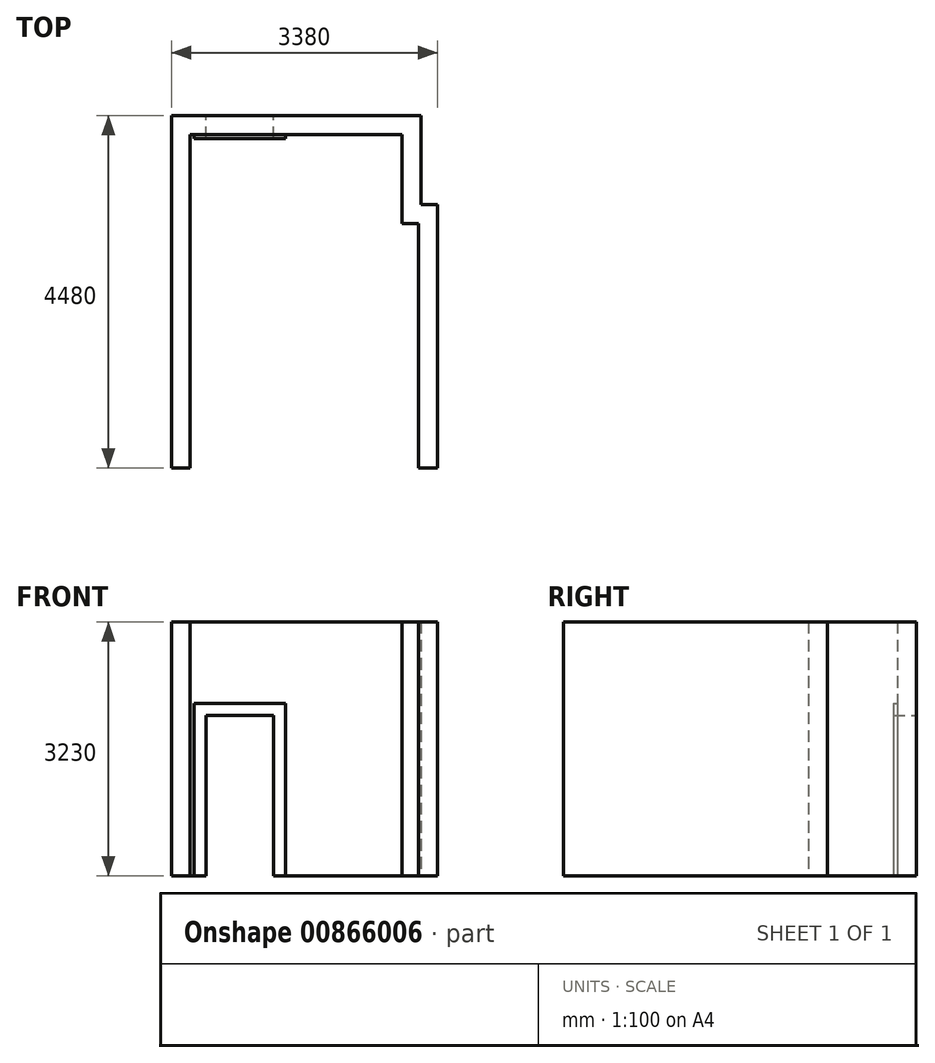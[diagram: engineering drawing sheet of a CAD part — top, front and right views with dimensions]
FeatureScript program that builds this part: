
annotation { "Feature Type Name" : "Feature", "Feature Type Description" : "" }
export const myFeature = defineFeature(function(context is Context, id is Id, definition is map)
    precondition{}
    {
        {
            var Q0;
            Q0=qCreatedBy(makeId("Top.planeOp"),FACE);
            var sketch = newSketch(context, id + "F0", { "sketchPlane" : qUnion([Q0])});
            skLineSegment(sketch, "E0.bottom", {"start": v(-3140, 4240) * mm, "end": v(-450, 4240) * mm});
            skLineSegment(sketch, "E0.top", {"start": v(-3140, 240) * mm, "end": v(-240, 240) * mm, "construction": true});
            skLineSegment(sketch, "E0.left", {"start": v(-3140, 4240) * mm, "end": v(-3140, 240) * mm});
            skLineSegment(sketch, "E0.right", {"start": v(-240, 3110) * mm, "end": v(-240, 240) * mm});
            skLineSegment(sketch, "E1", {"start": v(-450, 4240) * mm, "end": v(-450, 3110) * mm});
            skLineSegment(sketch, "E2", {"start": v(-450, 3110) * mm, "end": v(-240, 3110) * mm});
            skLineSegment(sketch, "E3", {"start": v(-3380, 4480) * mm, "end": v(-210, 4480) * mm});
            skLineSegment(sketch, "E4", {"start": v(-3380, 4480) * mm, "end": v(-3380, 0) * mm});
            skLineSegment(sketch, "E5", {"start": v(-3380, 0) * mm, "end": v(0, 0) * mm, "construction": true});
            skLineSegment(sketch, "E6", {"start": v(0, 0) * mm, "end": v(0, 3350) * mm});
            skLineSegment(sketch, "E7", {"start": v(0, 3350) * mm, "end": v(-210, 3350) * mm});
            skLineSegment(sketch, "E8", {"start": v(-210, 3350) * mm, "end": v(-210, 4480) * mm});
            skLineSegment(sketch, "E9", {"start": v(-240, 240) * mm, "end": v(-240, 0) * mm});
            skLineSegment(sketch, "E10", {"start": v(-3140, 240) * mm, "end": v(-3140, 0) * mm});
            skLineSegment(sketch, "E11", {"start": v(-240, 0) * mm, "end": v(0, 0) * mm});
            skLineSegment(sketch, "E12", {"start": v(-3140, 0) * mm, "end": v(-3380, 0) * mm});
            skSolve(sketch);
        }
        {
            var Q0;
            Q0 = qSketchRegion(id + "F0", true);
            extrude(context, id + "F1", {"entities" : qUnion([Q0]), "depth" : 3230 * mm, "offsetDistance" : 25 * mm});
        }
        {
            var Q0;
            Q0=makeQuery(id+"F1.opExtrude","SWEPT_FACE",FACE,{"disambiguationData":[OSD([sQuery(id+"F0.wireOp",EDGE,"E0.bottom")])]});
            var sketch = newSketch(context, id + "F2", { "sketchPlane" : qUnion([Q0])});
            skLineSegment(sketch, "E13.bottom", {"start": v(-3090, 2190) * mm, "end": v(-1930, 2190) * mm});
            skLineSegment(sketch, "E13.top", {"start": v(-3090, 0) * mm, "end": v(-2940, 0) * mm});
            skLineSegment(sketch, "E13.left", {"start": v(-3090, 2190) * mm, "end": v(-3090, 0) * mm});
            skLineSegment(sketch, "E13.right", {"start": v(-1930, 2190) * mm, "end": v(-1930, 0) * mm});
            skLineSegment(sketch, "E14", {"start": v(-2940, 2040) * mm, "end": v(-2080, 2040) * mm});
            skLineSegment(sketch, "E15", {"start": v(-2080, 2040) * mm, "end": v(-2080, 0) * mm});
            skLineSegment(sketch, "E16", {"start": v(-2940, 2040) * mm, "end": v(-2940, 0) * mm});
            skLineSegment(sketch, "E17.trimOffspring", {"start": v(-2080, 0) * mm, "end": v(-1930, 0) * mm});
            skSolve(sketch);
        }
        {
            var Q0;
            Q0 = qSketchRegion(id + "F2", true);
            extrude(context, id + "F3", {"entities" : qUnion([Q0]), "operationType" : NewBodyOperationType.ADD, "depth" : 50 * mm, "offsetDistance" : 25 * mm});
        }
        {
            var Q0;
            {var subQ0=sQuery(id+"F0.wireOp",EDGE,"E1");var subQ13=sQuery(id+"F0.wireOp",EDGE,"E0.bottom");Q0=makeQuery(id+"F3.boolean.opBoolean","SPLIT",FACE,{"disambiguationData":[TD([makeQuery(id+"F1.opExtrude","SWEPT_FACE",FACE,{"disambiguationData":[OSD([subQ0])]})])],"derivedFrom":makeQuery(id+"F1.opExtrude","SWEPT_FACE",FACE,{"disambiguationData":[OSD([subQ13])]})});}
            var sketch = newSketch(context, id + "F4", { "sketchPlane" : qUnion([Q0])});
            skLineSegment(sketch, "E18.0", {"start": v(-2940, 2040) * mm, "end": v(-2940, 0) * mm});
            skLineSegment(sketch, "E19.0", {"start": v(-2940, 2040) * mm, "end": v(-2080, 2040) * mm});
            skLineSegment(sketch, "E20.0", {"start": v(-2080, 2040) * mm, "end": v(-2080, 0) * mm});
            skLineSegment(sketch, "E21.0", {"start": v(-2940, 0) * mm, "end": v(-2080, 0) * mm});
            skSolve(sketch);
        }
        {
            var Q0;
            Q0 = qSketchRegion(id + "F4", true);
            extrude(context, id + "F5", {"entities" : qUnion([Q0]), "operationType" : NewBodyOperationType.REMOVE, "oppositeDirection" : true, "depth" : 300 * mm, "offsetDistance" : 25 * mm});
        }
    });
